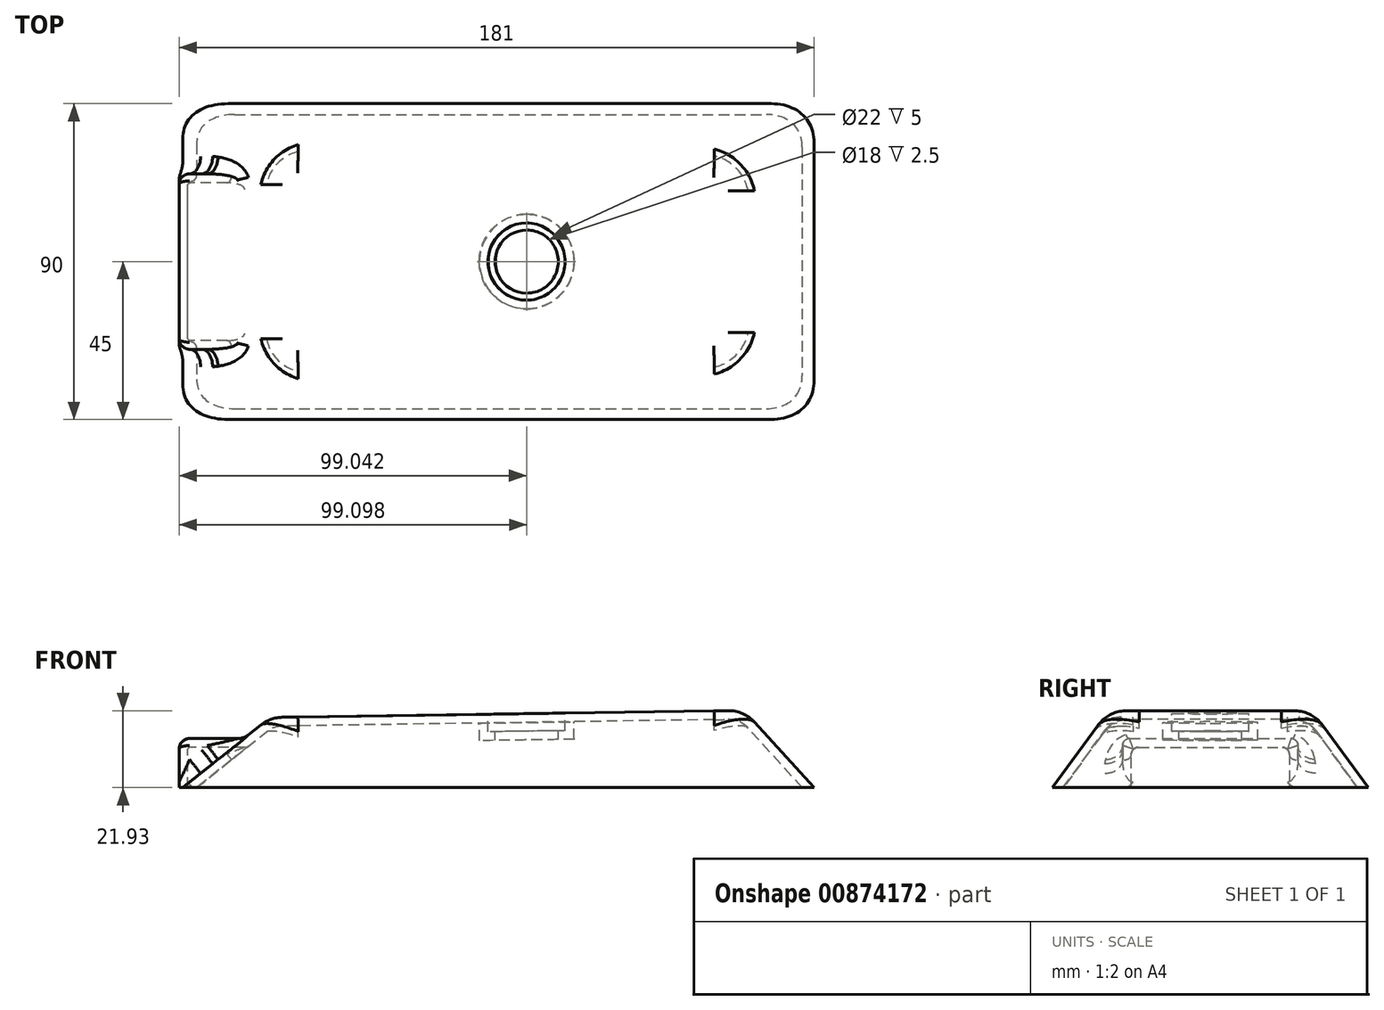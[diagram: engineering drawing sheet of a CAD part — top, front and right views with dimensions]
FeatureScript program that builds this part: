
annotation { "Feature Type Name" : "Feature", "Feature Type Description" : "" }
export const myFeature = defineFeature(function(context is Context, id is Id, definition is map)
    precondition{}
    {
        {
            var Q0;
            Q0=qCreatedBy(makeId("Top.planeOp"),FACE);
            var sketch = newSketch(context, id + "F0", { "sketchPlane" : qUnion([Q0])});
            skLineSegment(sketch, "E0.bottom", {"start": v(-85.92, 45) * mm, "end": v(94.08, 45) * mm});
            skLineSegment(sketch, "E0.top", {"start": v(-85.92, -45) * mm, "end": v(94.08, -45) * mm});
            skLineSegment(sketch, "E0.left", {"start": v(-85.92, 45) * mm, "end": v(-85.92, -45) * mm});
            skLineSegment(sketch, "E0.right", {"start": v(94.08, 45) * mm, "end": v(94.08, -45) * mm});
            skSolve(sketch);
        }
        {
            var Q0;
            Q0=makeQuery(id+"F0.imprint","IMPRINT",FACE,{"disambiguationData":[TD([[makeQuery(id+"F0.imprint","IMPRINT",EDGE,{"derivedFrom":sQuery(id+"F0.wireOp",EDGE,"E0.bottom")}),-1.0]])]});
            extrude(context, id + "F1", {"entities" : qUnion([Q0]), "depth" : 25 * mm, "offsetDistance" : 25 * mm});
        }
        {
            var Q0;
            Q0=makeQuery(id+"F1.opExtrude","SWEPT_FACE",FACE,{"disambiguationData":[OSD([sQuery(id+"F0.wireOp",EDGE,"E0.top")])]});
            var sketch = newSketch(context, id + "F2", { "sketchPlane" : qUnion([Q0])});
            skLineSegment(sketch, "E1", {"start": v(94.08, 0) * mm, "end": v(94.08, 25) * mm});
            skLineSegment(sketch, "E2", {"start": v(74.08, 22) * mm, "end": v(94.08, 0) * mm});
            skLineSegment(sketch, "E3", {"start": v(-85.92, 0) * mm, "end": v(-60.92, 20) * mm});
            skLineSegment(sketch, "E4", {"start": v(-60.92, 20) * mm, "end": v(74.08, 22) * mm});
            skLineSegment(sketch, "E5", {"start": v(-85.92, 0) * mm, "end": v(-85.92, 25) * mm});
            skLineSegment(sketch, "E6", {"start": v(-85.92, 25) * mm, "end": v(94.08, 25) * mm});
            skSolve(sketch);
        }
        {
            var Q0;
            Q0=makeQuery(id+"F1.opExtrude","SWEPT_FACE",FACE,{"disambiguationData":[OSD([sQuery(id+"F0.wireOp",EDGE,"E0.right")])]});
            var sketch = newSketch(context, id + "F3", { "sketchPlane" : qUnion([Q0])});
            skLineSegment(sketch, "E7", {"start": v(-45, 0) * mm, "end": v(-29, 22) * mm});
            skLineSegment(sketch, "E8", {"start": v(-29, 22) * mm, "end": v(29, 22) * mm});
            skLineSegment(sketch, "E9", {"start": v(29, 22) * mm, "end": v(45, 0) * mm});
            skLineSegment(sketch, "E10", {"start": v(45, 0) * mm, "end": v(45, 25) * mm});
            skLineSegment(sketch, "E11", {"start": v(45, 25) * mm, "end": v(-45, 25) * mm});
            skLineSegment(sketch, "E12", {"start": v(-45, 25) * mm, "end": v(-45, 0) * mm});
            skSolve(sketch);
        }
        {
            var Q0;
            Q0=makeQuery(id+"F3.imprint","IMPRINT",FACE,{"disambiguationData":[TD([[makeQuery(id+"F3.imprint","IMPRINT",EDGE,{"derivedFrom":sQuery(id+"F3.wireOp",EDGE,"E7")}),1.0]])]});
            extrude(context, id + "F4", {"entities" : qUnion([Q0]), "operationType" : NewBodyOperationType.REMOVE, "endBound" : BoundingType.THROUGH_ALL, "oppositeDirection" : true, "depth" : 25 * mm, "offsetDistance" : 25 * mm});
        }
        {
            var Q0;
            Q0=makeQuery(id+"F2.imprint","IMPRINT",FACE,{"disambiguationData":[TD([[makeQuery(id+"F2.imprint","IMPRINT",EDGE,{"derivedFrom":sQuery(id+"F2.wireOp",EDGE,"E1")}),-1.0]])]});
            extrude(context, id + "F5", {"entities" : qUnion([Q0]), "operationType" : NewBodyOperationType.REMOVE, "endBound" : BoundingType.THROUGH_ALL, "oppositeDirection" : true, "depth" : 25 * mm, "offsetDistance" : 25 * mm});
        }
        {
            var Q0;
            Q0=qCreatedBy(makeId("Front.planeOp"),FACE);
            var sketch = newSketch(context, id + "F6", { "sketchPlane" : qUnion([Q0])});
            skLineSegment(sketch, "E13.bottom", {"start": v(-65.92, 0) * mm, "end": v(-86.92, 0) * mm});
            skLineSegment(sketch, "E13.top", {"start": v(-65.92, 14) * mm, "end": v(-86.92, 14) * mm});
            skLineSegment(sketch, "E13.left", {"start": v(-65.92, 0) * mm, "end": v(-65.92, 14) * mm});
            skLineSegment(sketch, "E13.right", {"start": v(-86.92, 0) * mm, "end": v(-86.92, 14) * mm});
            skSolve(sketch);
        }
        {
            var Q0;
            Q0=makeQuery(id+"F6.imprint","IMPRINT",FACE,{"disambiguationData":[TD([[makeQuery(id+"F6.imprint","IMPRINT",EDGE,{"derivedFrom":sQuery(id+"F6.wireOp",EDGE,"E13.bottom")}),-1.0]])]});
            extrude(context, id + "F7", {"entities" : qUnion([Q0]), "operationType" : NewBodyOperationType.ADD, "depth" : 25 * mm, "offsetDistance" : 25 * mm, "hasSecondDirection" : true, "secondDirectionOppositeDirection" : true, "secondDirectionDepth" : 25 * mm});
        }
        {
            var Q0;
            Q0=makeQuery(id+"F5.boolean.opBoolean","COPY",FACE,{"derivedFrom":makeQuery(id+"F5.opExtrude","SWEPT_FACE",FACE,{"disambiguationData":[OSD([sQuery(id+"F2.wireOp",EDGE,"E4")])]})});
            var sketch = newSketch(context, id + "F8", { "sketchPlane" : qUnion([Q0])});
            skCircle(sketch, "E14", {"center": v(12.4, 0) * mm, "radius": 11 * mm});
            skSolve(sketch);
        }
        {
            var Q0;
            Q0=makeQuery(id+"F8.imprint","IMPRINT",FACE,{"disambiguationData":[TD([[makeQuery(id+"F8.imprint","IMPRINT",EDGE,{"derivedFrom":sQuery(id+"F8.wireOp",EDGE,"E14")}),1.0]])]});
            extrude(context, id + "F9", {"entities" : qUnion([Q0]), "operationType" : NewBodyOperationType.REMOVE, "oppositeDirection" : true, "depth" : 5 * mm, "offsetDistance" : 25 * mm});
        }
        {
            var Q0;
            Q0=makeQuery(id+"F9.boolean.opBoolean","COPY",FACE,{"derivedFrom":makeQuery(id+"F9.opExtrude","CAP_FACE",FACE,{"disambiguationData":[OSD([sQuery(id+"F8.wireOp",EDGE,"E14")])],"isStart":false})});
            var sketch = newSketch(context, id + "F10", { "sketchPlane" : qUnion([Q0])});
            skCircle(sketch, "E15", {"center": v(12.4, 0) * mm, "radius": 9 * mm});
            skSolve(sketch);
        }
        {
            var Q0;
            Q0=makeQuery(id+"F7.opExtrude","CAP_EDGE",EDGE,{"disambiguationData":[OSD([sQuery(id+"F6.wireOp",EDGE,"E13.top")])],"isStart":false});
            var Q1;
            Q1=makeQuery(id+"F7.opExtrude","CAP_EDGE",EDGE,{"disambiguationData":[OSD([sQuery(id+"F6.wireOp",EDGE,"E13.top")])],"isStart":true});
            fillet(context, id + "F11", {"entities" : qUnion([Q0, Q1]), "radius" : 2 * mm, "tangentPropagation" : true, "allowEdgeOverflow" : false});
        }
        {
            var Q0;
            Q0=makeQuery(id+"F5.boolean.opBoolean","INTERSECT",EDGE,{"derivedFrom":[makeQuery(id+"F4.boolean.opBoolean","COPY",FACE,{"derivedFrom":makeQuery(id+"F4.opExtrude","SWEPT_FACE",FACE,{"disambiguationData":[OSD([sQuery(id+"F3.wireOp",EDGE,"E9")])]})}),makeQuery(id+"F5.opExtrude","SWEPT_FACE",FACE,{"disambiguationData":[OSD([sQuery(id+"F2.wireOp",EDGE,"E4")])]})]});
            var Q1;
            Q1=makeQuery(id+"F5.boolean.opBoolean","COPY",EDGE,{"derivedFrom":makeQuery(id+"F5.opExtrude","SWEPT_EDGE",EDGE,{"disambiguationData":[OSD([sQuery(id+"F2.wireOp",EDGE,"E3"),sQuery(id+"F2.wireOp",EDGE,"E4")])]})});
            var Q2;
            Q2=makeQuery(id+"F5.boolean.opBoolean","INTERSECT",EDGE,{"derivedFrom":[makeQuery(id+"F4.boolean.opBoolean","COPY",FACE,{"derivedFrom":makeQuery(id+"F4.opExtrude","SWEPT_FACE",FACE,{"disambiguationData":[OSD([sQuery(id+"F3.wireOp",EDGE,"E7")])]})}),makeQuery(id+"F5.opExtrude","SWEPT_FACE",FACE,{"disambiguationData":[OSD([sQuery(id+"F2.wireOp",EDGE,"E4")])]})]});
            var Q3;
            Q3=makeQuery(id+"F5.boolean.opBoolean","COPY",EDGE,{"derivedFrom":makeQuery(id+"F5.opExtrude","SWEPT_EDGE",EDGE,{"disambiguationData":[OSD([sQuery(id+"F2.wireOp",EDGE,"E2"),sQuery(id+"F2.wireOp",EDGE,"E4")])]})});
            fillet(context, id + "F12", {"entities" : qUnion([Q0, Q1, Q2, Q3]), "radius" : 10 * mm, "tangentPropagation" : true, "allowEdgeOverflow" : false});
        }
        {
            var Q0;
            Q0=makeQuery(id+"F7.opExtrude","SWEPT_EDGE",EDGE,{"disambiguationData":[OSD([sQuery(id+"F6.wireOp",EDGE,"E13.top"),sQuery(id+"F6.wireOp",EDGE,"E13.right")])]});
            fillet(context, id + "F13", {"entities" : qUnion([Q0]), "radius" : 3 * mm, "tangentPropagation" : true, "allowEdgeOverflow" : false});
        }
        {
            var Q0;
            Q0=makeQuery(id+"F5.boolean.opBoolean","INTERSECT",EDGE,{"derivedFrom":[makeQuery(id+"F4.boolean.opBoolean","COPY",FACE,{"derivedFrom":makeQuery(id+"F4.opExtrude","SWEPT_FACE",FACE,{"disambiguationData":[OSD([sQuery(id+"F3.wireOp",EDGE,"E9")])]})}),makeQuery(id+"F5.opExtrude","SWEPT_FACE",FACE,{"disambiguationData":[OSD([sQuery(id+"F2.wireOp",EDGE,"E3")])]})]});
            var Q1;
            Q1=makeQuery(id+"F5.boolean.opBoolean","INTERSECT",EDGE,{"derivedFrom":[makeQuery(id+"F4.boolean.opBoolean","COPY",FACE,{"derivedFrom":makeQuery(id+"F4.opExtrude","SWEPT_FACE",FACE,{"disambiguationData":[OSD([sQuery(id+"F3.wireOp",EDGE,"E7")])]})}),makeQuery(id+"F5.opExtrude","SWEPT_FACE",FACE,{"disambiguationData":[OSD([sQuery(id+"F2.wireOp",EDGE,"E3")])]})]});
            var Q2;
            Q2=makeQuery(id+"F5.boolean.opBoolean","INTERSECT",EDGE,{"derivedFrom":[makeQuery(id+"F4.boolean.opBoolean","COPY",FACE,{"derivedFrom":makeQuery(id+"F4.opExtrude","SWEPT_FACE",FACE,{"disambiguationData":[OSD([sQuery(id+"F3.wireOp",EDGE,"E7")])]})}),makeQuery(id+"F5.opExtrude","SWEPT_FACE",FACE,{"disambiguationData":[OSD([sQuery(id+"F2.wireOp",EDGE,"E2")])]})]});
            var Q3;
            Q3=makeQuery(id+"F5.boolean.opBoolean","INTERSECT",EDGE,{"derivedFrom":[makeQuery(id+"F4.boolean.opBoolean","COPY",FACE,{"derivedFrom":makeQuery(id+"F4.opExtrude","SWEPT_FACE",FACE,{"disambiguationData":[OSD([sQuery(id+"F3.wireOp",EDGE,"E9")])]})}),makeQuery(id+"F5.opExtrude","SWEPT_FACE",FACE,{"disambiguationData":[OSD([sQuery(id+"F2.wireOp",EDGE,"E2")])]})]});
            fillet(context, id + "F14", {"entities" : qUnion([Q0, Q1, Q2, Q3]), "radius" : 15 * mm, "tangentPropagation" : true, "allowEdgeOverflow" : false});
        }
        {
            var Q0;
            Q0=makeQuery(id+"F7.boolean.opBoolean","MERGE",FACE,{"derivedFrom":[makeQuery(id+"F1.opExtrude","CAP_FACE",FACE,{"disambiguationData":[OSD([sQuery(id+"F0.wireOp",EDGE,"E0.bottom"),sQuery(id+"F0.wireOp",EDGE,"E0.top"),sQuery(id+"F0.wireOp",EDGE,"E0.left"),sQuery(id+"F0.wireOp",EDGE,"E0.right")])],"isStart":true}),makeQuery(id+"F7.opExtrude","SWEPT_FACE",FACE,{"disambiguationData":[OSD([sQuery(id+"F6.wireOp",EDGE,"E13.bottom")])]})]});
            shell(context, id + "F15", {"entities" : qUnion([Q0]), "thickness" : 2.5 * mm});
        }
        {
            var Q0;
            Q0=makeQuery(id+"F10.imprint","IMPRINT",FACE,{"disambiguationData":[TD([[makeQuery(id+"F10.imprint","IMPRINT",EDGE,{"derivedFrom":sQuery(id+"F10.wireOp",EDGE,"E15")}),1.0]])]});
            extrude(context, id + "F16", {"entities" : qUnion([Q0]), "operationType" : NewBodyOperationType.REMOVE, "oppositeDirection" : true, "depth" : 25 * mm, "offsetDistance" : 25 * mm});
        }
        {
            var Q0;
            Q0=makeQuery(id+"F7.boolean.opBoolean","INTERSECT",EDGE,{"derivedFrom":[makeQuery(id+"F5.boolean.opBoolean","COPY",FACE,{"derivedFrom":makeQuery(id+"F5.opExtrude","SWEPT_FACE",FACE,{"disambiguationData":[OSD([sQuery(id+"F2.wireOp",EDGE,"E3")])]})}),makeQuery(id+"F7.opExtrude","SWEPT_FACE",FACE,{"disambiguationData":[OSD([sQuery(id+"F6.wireOp",EDGE,"E13.top")])]})]});
            fillet(context, id + "F17", {"entities" : qUnion([Q0]), "radius" : 5 * mm, "tangentPropagation" : true, "allowEdgeOverflow" : false});
        }
        {
            var Q0;
            {var subQ0=sQuery(id+"F6.wireOp",EDGE,"E13.right");var subQ1=sQuery(id+"F6.wireOp",EDGE,"E13.left");var subQ2=sQuery(id+"F6.wireOp",EDGE,"E13.top");var subQ3=sQuery(id+"F6.wireOp",EDGE,"E13.bottom");var subQ4=sQuery(id+"F2.wireOp",EDGE,"E3");Q0=makeQuery(id+"F15.opShell","OFFSET_EDGE",EDGE,{"disambiguationData":[OSD([subQ4,subQ3,subQ2,subQ1,subQ0]),TDD([makeQuery(id+"F7.boolean.opBoolean","INTERSECT",EDGE,{"derivedFrom":[makeQuery(id+"F5.boolean.opBoolean","COPY",FACE,{"derivedFrom":makeQuery(id+"F5.opExtrude","SWEPT_FACE",FACE,{"disambiguationData":[OSD([subQ4])]})}),makeQuery(id+"F7.opExtrude","CAP_FACE",FACE,{"disambiguationData":[OSD([subQ3,subQ2,subQ1,subQ0])],"isStart":false})]})])]});}
            var Q1;
            Q1=makeQuery(id+"F15.opShell","OFFSET_EDGE",EDGE,{"disambiguationData":[OSD([sQuery(id+"F2.wireOp",EDGE,"E3"),sQuery(id+"F6.wireOp",EDGE,"E13.top")])]});
            var Q2;
            {var subQ0=sQuery(id+"F6.wireOp",EDGE,"E13.right");var subQ1=sQuery(id+"F6.wireOp",EDGE,"E13.left");var subQ2=sQuery(id+"F6.wireOp",EDGE,"E13.top");var subQ3=sQuery(id+"F6.wireOp",EDGE,"E13.bottom");var subQ4=sQuery(id+"F2.wireOp",EDGE,"E3");Q2=makeQuery(id+"F15.opShell","OFFSET_EDGE",EDGE,{"disambiguationData":[OSD([subQ4,subQ3,subQ2,subQ1,subQ0]),TDD([makeQuery(id+"F7.boolean.opBoolean","INTERSECT",EDGE,{"derivedFrom":[makeQuery(id+"F5.boolean.opBoolean","COPY",FACE,{"derivedFrom":makeQuery(id+"F5.opExtrude","SWEPT_FACE",FACE,{"disambiguationData":[OSD([subQ4])]})}),makeQuery(id+"F7.opExtrude","CAP_FACE",FACE,{"disambiguationData":[OSD([subQ3,subQ2,subQ1,subQ0])],"isStart":true})]})])]});}
            var Q3;
            {var subQ0=sQuery(id+"F6.wireOp",EDGE,"E13.right");var subQ1=sQuery(id+"F6.wireOp",EDGE,"E13.left");var subQ2=sQuery(id+"F6.wireOp",EDGE,"E13.top");var subQ3=sQuery(id+"F6.wireOp",EDGE,"E13.bottom");var subQ4=makeQuery(id+"F7.opExtrude","CAP_EDGE",EDGE,{"disambiguationData":[OSD([subQ2])],"isStart":false});Q3=makeQuery(id+"F15.opShell","OFFSET_EDGE",EDGE,{"disambiguationData":[OSD([subQ3,subQ2,subQ1,subQ0]),TDD([makeQuery(id+"F11.opFillet","BLEND_EDGE",EDGE,{"blendedFrom":[subQ4,makeQuery(id+"F7.opExtrude","SWEPT_FACE",FACE,{"disambiguationData":[OSD([subQ2])]})],"blendedInto":[makeQuery(id+"F7.opExtrude","SWEPT_FACE",FACE,{"disambiguationData":[OSD([subQ2])]})]}),makeQuery(id+"F11.opFillet","BLEND_EDGE",EDGE,{"blendedFrom":[subQ4,makeQuery(id+"F7.opExtrude","CAP_FACE",FACE,{"disambiguationData":[OSD([subQ3,subQ2,subQ1,subQ0])],"isStart":false})],"blendedInto":[makeQuery(id+"F7.opExtrude","CAP_FACE",FACE,{"disambiguationData":[OSD([subQ3,subQ2,subQ1,subQ0])],"isStart":false})]})])]});}
            var Q4;
            {var subQ0=sQuery(id+"F6.wireOp",EDGE,"E13.top");var subQ1=makeQuery(id+"F7.opExtrude","CAP_EDGE",EDGE,{"disambiguationData":[OSD([subQ0])],"isStart":true});var subQ2=sQuery(id+"F6.wireOp",EDGE,"E13.right");var subQ3=sQuery(id+"F6.wireOp",EDGE,"E13.left");var subQ4=sQuery(id+"F6.wireOp",EDGE,"E13.bottom");Q4=makeQuery(id+"F15.opShell","OFFSET_EDGE",EDGE,{"disambiguationData":[OSD([subQ4,subQ0,subQ3,subQ2]),TDD([makeQuery(id+"F11.opFillet","BLEND_EDGE",EDGE,{"blendedFrom":[subQ1,makeQuery(id+"F7.opExtrude","CAP_FACE",FACE,{"disambiguationData":[OSD([subQ4,subQ0,subQ3,subQ2])],"isStart":true})],"blendedInto":[makeQuery(id+"F7.opExtrude","CAP_FACE",FACE,{"disambiguationData":[OSD([subQ4,subQ0,subQ3,subQ2])],"isStart":true})]}),makeQuery(id+"F11.opFillet","BLEND_EDGE",EDGE,{"blendedFrom":[subQ1,makeQuery(id+"F7.opExtrude","SWEPT_FACE",FACE,{"disambiguationData":[OSD([subQ0])]})],"blendedInto":[makeQuery(id+"F7.opExtrude","SWEPT_FACE",FACE,{"disambiguationData":[OSD([subQ0])]})]})])]});}
            fillet(context, id + "F18", {"entities" : qUnion([Q0, Q1, Q2, Q3, Q4]), "radius" : 2 * mm, "tangentPropagation" : true, "allowEdgeOverflow" : false});
        }
    });
